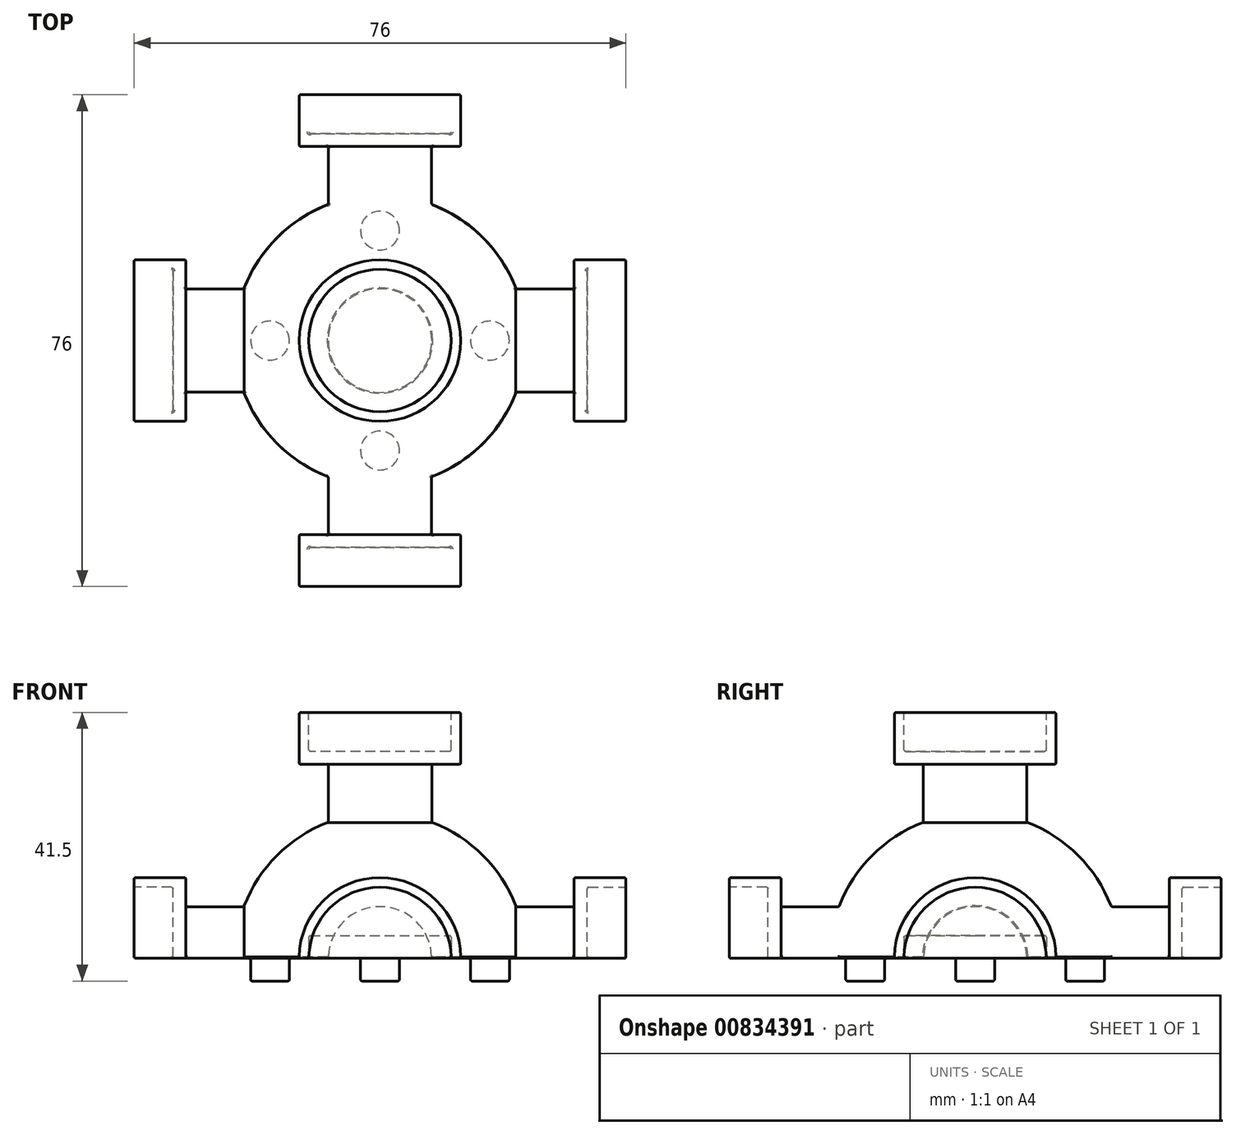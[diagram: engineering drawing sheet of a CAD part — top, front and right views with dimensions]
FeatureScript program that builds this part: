
annotation { "Feature Type Name" : "Feature", "Feature Type Description" : "" }
export const myFeature = defineFeature(function(context is Context, id is Id, definition is map)
    precondition{}
    {
        {
            var Q0;
            Q0=qCreatedBy(makeId("Top.planeOp"),FACE);
            var sketch = newSketch(context, id + "F0", { "sketchPlane" : qUnion([Q0])});
            skCircle(sketch, "E0", {"center": v(0, 0) * mm, "radius": 22.5 * mm});
            skLineSegment(sketch, "E1", {"start": v(0, 22.5) * mm, "end": v(0, -22.5) * mm});
            skSolve(sketch);
        }
        {
            var Q0;
            {var subQ0=sQuery(id+"F0.wireOp",EDGE,"E1");Q0=makeQuery(id+"F0.imprint","IMPRINT",FACE,{"disambiguationData":[TD([[makeQuery(id+"F0.imprint","IMPRINT",EDGE,{"derivedFrom":subQ0}),1.0]])]});}
            var Q1;
            Q1=sQuery(id+"F0.wireOp",EDGE,"E1");
            revolve(context, id + "F1", {"surfaceOperationType" : NewSurfaceOperationType.NEW, "entities" : qUnion([Q0]), "axis" : qUnion([Q1]), "revolveType" : RevolveType.ONE_DIRECTION, "angle" : 180 * degree});
        }
        {
            var Q0;
            Q0=makeQuery(id+"F1.opRevolve","CAP_FACE",FACE,{"disambiguationData":[OSD([sQuery(id+"F0.wireOp",EDGE,"E0"),sQuery(id+"F0.wireOp",EDGE,"E1")])],"isStart":true});
            var sketch = newSketch(context, id + "F2", { "sketchPlane" : qUnion([Q0])});
            skCircle(sketch, "E2", {"center": v(0, 0) * mm, "radius": 11 * mm});
            skSolve(sketch);
        }
        {
            var Q0;
            Q0 = qSketchRegion(id + "F2", true);
            extrude(context, id + "F3", {"entities" : qUnion([Q0]), "operationType" : NewBodyOperationType.REMOVE, "oppositeDirection" : true, "depth" : 3.5 * mm, "offsetDistance" : 25 * mm});
        }
        {
            var Q0;
            Q0=makeQuery(id+"F1.opRevolve","CAP_FACE",FACE,{"disambiguationData":[OSD([sQuery(id+"F0.wireOp",EDGE,"E0"),sQuery(id+"F0.wireOp",EDGE,"E1")])],"isStart":true});
            var sketch = newSketch(context, id + "F4", { "sketchPlane" : qUnion([Q0])});
            skCircle(sketch, "E3", {"center": v(0, 17) * mm, "radius": 3 * mm});
            skCircle(sketch, "E4", {"center": v(17, 0) * mm, "radius": 3 * mm});
            skCircle(sketch, "E5.MirrorC", {"center": v(-17, 0) * mm, "radius": 3 * mm});
            skCircle(sketch, "E6.MirrorC", {"center": v(0, -17) * mm, "radius": 3 * mm});
            skPoint(sketch, "E7.orphan", {"position": v(0, 0) * mm});
            skSolve(sketch);
        }
        {
            var Q0;
            Q0 = qSketchRegion(id + "F4", true);
            extrude(context, id + "F5", {"entities" : qUnion([Q0]), "operationType" : NewBodyOperationType.ADD, "depth" : 3.5 * mm, "offsetDistance" : 25 * mm});
        }
        {
            var Q0;
            Q0=qCreatedBy(makeId("Top.planeOp"),FACE);
            cPlane(context, id + "F6", {"entities" : qUnion([Q0]), "cplaneType" : CPlaneType.OFFSET, "offset" : 20 * mm, "width" : 150 * mm, "height" : 150 * mm});
        }
        {
            var Q0;
            Q0=qCreatedBy(id+"F6.planeOp",FACE);
            var sketch = newSketch(context, id + "F7", { "sketchPlane" : qUnion([Q0])});
            skCircle(sketch, "E8", {"center": v(0, 0) * mm, "radius": 8 * mm});
            skSolve(sketch);
        }
        {
            var Q0;
            Q0 = qSketchRegion(id + "F7", true);
            extrude(context, id + "F8", {"entities" : qUnion([Q0]), "operationType" : NewBodyOperationType.ADD, "depth" : 10 * mm, "offsetDistance" : 25 * mm});
        }
        {
            var Q0;
            Q0=makeQuery(id+"F8.opExtrude","CAP_FACE",FACE,{"disambiguationData":[OSD([sQuery(id+"F7.wireOp",EDGE,"E8")])],"isStart":false});
            var sketch = newSketch(context, id + "F9", { "sketchPlane" : qUnion([Q0])});
            skCircle(sketch, "E9", {"center": v(0, 0) * mm, "radius": 12.5 * mm});
            skSolve(sketch);
        }
        {
            var Q0;
            Q0 = qSketchRegion(id + "F9", true);
            extrude(context, id + "F10", {"entities" : qUnion([Q0]), "operationType" : NewBodyOperationType.ADD, "depth" : 8 * mm, "offsetDistance" : 25 * mm});
        }
        {
            var Q0;
            Q0=makeQuery(id+"F10.opExtrude","CAP_FACE",FACE,{"disambiguationData":[OSD([sQuery(id+"F9.wireOp",EDGE,"E9")])],"isStart":false});
            var sketch = newSketch(context, id + "F11", { "sketchPlane" : qUnion([Q0])});
            skCircle(sketch, "E10", {"center": v(0, 0) * mm, "radius": 11 * mm});
            skSolve(sketch);
        }
        {
            var Q0;
            Q0 = qSketchRegion(id + "F11", true);
            extrude(context, id + "F12", {"entities" : qUnion([Q0]), "operationType" : NewBodyOperationType.REMOVE, "oppositeDirection" : true, "depth" : 6 * mm, "offsetDistance" : 25 * mm});
        }
        {
            var Q0;
            Q0=qCreatedBy(makeId("Right.planeOp"),FACE);
            cPlane(context, id + "F13", {"entities" : qUnion([Q0]), "cplaneType" : CPlaneType.OFFSET, "offset" : 20 * mm, "width" : 150 * mm, "height" : 150 * mm});
        }
        {
            var Q0;
            Q0=qCreatedBy(id+"F13.planeOp",FACE);
            var sketch = newSketch(context, id + "F14", { "sketchPlane" : qUnion([Q0])});
            skArc(sketch, "E11", {"start": v(8, 0) * mm, "mid": v(0, 8) * mm, "end": v(-8, 0) * mm});
            skLineSegment(sketch, "E12", {"start": v(-8, 0) * mm, "end": v(8, 0) * mm});
            skSolve(sketch);
        }
        {
            var Q0;
            Q0 = qSketchRegion(id + "F14", true);
            extrude(context, id + "F15", {"entities" : qUnion([Q0]), "operationType" : NewBodyOperationType.ADD, "depth" : 10 * mm, "offsetDistance" : 25 * mm});
        }
        {
            var Q0;
            Q0=makeQuery(id+"F15.opExtrude","CAP_FACE",FACE,{"disambiguationData":[OSD([sQuery(id+"F14.wireOp",EDGE,"E11"),sQuery(id+"F14.wireOp",EDGE,"E12")])],"isStart":false});
            var sketch = newSketch(context, id + "F16", { "sketchPlane" : qUnion([Q0])});
            skArc(sketch, "E13", {"start": v(12.5, 0) * mm, "mid": v(0, 12.5) * mm, "end": v(-12.5, 0) * mm});
            skLineSegment(sketch, "E14", {"start": v(-12.5, 0) * mm, "end": v(12.5, 0) * mm});
            skSolve(sketch);
        }
        {
            var Q0;
            Q0 = qSketchRegion(id + "F16", true);
            extrude(context, id + "F17", {"entities" : qUnion([Q0]), "operationType" : NewBodyOperationType.ADD, "depth" : 8 * mm, "offsetDistance" : 25 * mm});
        }
        {
            var Q0;
            Q0=makeQuery(id+"F17.opExtrude","CAP_FACE",FACE,{"disambiguationData":[OSD([sQuery(id+"F16.wireOp",EDGE,"E13"),sQuery(id+"F16.wireOp",EDGE,"E14")])],"isStart":false});
            var sketch = newSketch(context, id + "F18", { "sketchPlane" : qUnion([Q0])});
            skArc(sketch, "E15", {"start": v(11, 0) * mm, "mid": v(0, 11) * mm, "end": v(-11, 0) * mm});
            skLineSegment(sketch, "E16", {"start": v(-11, 0) * mm, "end": v(11, 0) * mm});
            skSolve(sketch);
        }
        {
            var Q0;
            Q0 = qSketchRegion(id + "F18", true);
            extrude(context, id + "F19", {"entities" : qUnion([Q0]), "operationType" : NewBodyOperationType.REMOVE, "oppositeDirection" : true, "depth" : 6 * mm, "offsetDistance" : 25 * mm});
        }
        {
            var Q0;
            Q0=qCreatedBy(makeId("Front.planeOp"),FACE);
            cPlane(context, id + "F20", {"entities" : qUnion([Q0]), "cplaneType" : CPlaneType.OFFSET, "offset" : 20 * mm, "oppositeDirection" : true, "width" : 150 * mm, "height" : 150 * mm});
        }
        {
            var Q0;
            Q0=qCreatedBy(id+"F20.planeOp",FACE);
            var sketch = newSketch(context, id + "F21", { "sketchPlane" : qUnion([Q0])});
            skArc(sketch, "E17", {"start": v(8, 0) * mm, "mid": v(0, 8) * mm, "end": v(-8, 0) * mm});
            skLineSegment(sketch, "E18", {"start": v(8, 0) * mm, "end": v(-8, 0) * mm});
            skSolve(sketch);
        }
        {
            var Q0;
            Q0 = qSketchRegion(id + "F21", true);
            extrude(context, id + "F22", {"entities" : qUnion([Q0]), "operationType" : NewBodyOperationType.ADD, "oppositeDirection" : true, "depth" : 10 * mm, "offsetDistance" : 25 * mm});
        }
        {
            var Q0;
            Q0=makeQuery(id+"F22.opExtrude","CAP_FACE",FACE,{"disambiguationData":[OSD([sQuery(id+"F21.wireOp",EDGE,"E17"),sQuery(id+"F21.wireOp",EDGE,"E18")])],"isStart":false});
            var sketch = newSketch(context, id + "F23", { "sketchPlane" : qUnion([Q0])});
            skArc(sketch, "E19", {"start": v(12.5, 0) * mm, "mid": v(0, 12.5) * mm, "end": v(-12.5, 0) * mm});
            skLineSegment(sketch, "E20", {"start": v(-12.5, 0) * mm, "end": v(12.5, 0) * mm});
            skSolve(sketch);
        }
        {
            var Q0;
            Q0 = qSketchRegion(id + "F23", true);
            extrude(context, id + "F24", {"entities" : qUnion([Q0]), "operationType" : NewBodyOperationType.ADD, "depth" : 8 * mm, "offsetDistance" : 25 * mm});
        }
        {
            var Q0;
            Q0=makeQuery(id+"F24.opExtrude","CAP_FACE",FACE,{"disambiguationData":[OSD([sQuery(id+"F23.wireOp",EDGE,"E19"),sQuery(id+"F23.wireOp",EDGE,"E20")])],"isStart":false});
            var sketch = newSketch(context, id + "F25", { "sketchPlane" : qUnion([Q0])});
            skArc(sketch, "E21", {"start": v(11, 0) * mm, "mid": v(0, 11) * mm, "end": v(-11, 0) * mm});
            skLineSegment(sketch, "E22", {"start": v(-11, 0) * mm, "end": v(11, 0) * mm});
            skSolve(sketch);
        }
        {
            var Q0;
            Q0 = qSketchRegion(id + "F25", true);
            extrude(context, id + "F26", {"entities" : qUnion([Q0]), "operationType" : NewBodyOperationType.REMOVE, "oppositeDirection" : true, "depth" : 6 * mm, "offsetDistance" : 25 * mm});
        }
        {
            var Q0;
            Q0=qCreatedBy(makeId("Right.planeOp"),FACE);
            cPlane(context, id + "F27", {"entities" : qUnion([Q0]), "cplaneType" : CPlaneType.OFFSET, "offset" : 20 * mm, "oppositeDirection" : true, "width" : 150 * mm, "height" : 150 * mm});
        }
        {
            var Q0;
            Q0=qCreatedBy(id+"F27.planeOp",FACE);
            var sketch = newSketch(context, id + "F28", { "sketchPlane" : qUnion([Q0])});
            skArc(sketch, "E23", {"start": v(8, 0) * mm, "mid": v(0, 8) * mm, "end": v(-8, 0) * mm});
            skLineSegment(sketch, "E24", {"start": v(8, 0) * mm, "end": v(-8, 0) * mm});
            skSolve(sketch);
        }
        {
            var Q0;
            Q0 = qSketchRegion(id + "F28", true);
            extrude(context, id + "F29", {"entities" : qUnion([Q0]), "operationType" : NewBodyOperationType.ADD, "oppositeDirection" : true, "depth" : 10 * mm, "offsetDistance" : 25 * mm});
        }
        {
            var Q0;
            Q0=makeQuery(id+"F29.opExtrude","CAP_FACE",FACE,{"disambiguationData":[OSD([sQuery(id+"F28.wireOp",EDGE,"E23"),sQuery(id+"F28.wireOp",EDGE,"E24")])],"isStart":false});
            var sketch = newSketch(context, id + "F30", { "sketchPlane" : qUnion([Q0])});
            skArc(sketch, "E25", {"start": v(12.5, 0) * mm, "mid": v(0, 12.5) * mm, "end": v(-12.5, 0) * mm});
            skLineSegment(sketch, "E26", {"start": v(-12.5, 0) * mm, "end": v(12.5, 0) * mm});
            skSolve(sketch);
        }
        {
            var Q0;
            Q0 = qSketchRegion(id + "F30", true);
            extrude(context, id + "F31", {"entities" : qUnion([Q0]), "operationType" : NewBodyOperationType.ADD, "depth" : 8 * mm, "offsetDistance" : 25 * mm});
        }
        {
            var Q0;
            Q0=makeQuery(id+"F31.opExtrude","CAP_FACE",FACE,{"disambiguationData":[OSD([sQuery(id+"F30.wireOp",EDGE,"E25"),sQuery(id+"F30.wireOp",EDGE,"E26")])],"isStart":false});
            var sketch = newSketch(context, id + "F32", { "sketchPlane" : qUnion([Q0])});
            skArc(sketch, "E27", {"start": v(11, 0) * mm, "mid": v(0, 11) * mm, "end": v(-11, 0) * mm});
            skLineSegment(sketch, "E28", {"start": v(-11, 0) * mm, "end": v(11, 0) * mm});
            skSolve(sketch);
        }
        {
            var Q0;
            Q0 = qSketchRegion(id + "F32", true);
            extrude(context, id + "F33", {"entities" : qUnion([Q0]), "operationType" : NewBodyOperationType.REMOVE, "oppositeDirection" : true, "depth" : 6 * mm, "offsetDistance" : 25 * mm});
        }
        {
            var Q0;
            Q0=qCreatedBy(makeId("Front.planeOp"),FACE);
            cPlane(context, id + "F34", {"entities" : qUnion([Q0]), "cplaneType" : CPlaneType.OFFSET, "offset" : 20 * mm, "width" : 150 * mm, "height" : 150 * mm});
        }
        {
            var Q0;
            Q0=qCreatedBy(id+"F34.planeOp",FACE);
            var sketch = newSketch(context, id + "F35", { "sketchPlane" : qUnion([Q0])});
            skArc(sketch, "E29", {"start": v(8, 0) * mm, "mid": v(0, 8) * mm, "end": v(-8, 0) * mm});
            skLineSegment(sketch, "E30", {"start": v(-8, 0) * mm, "end": v(8, 0) * mm});
            skSolve(sketch);
        }
        {
            var Q0;
            Q0 = qSketchRegion(id + "F35", true);
            extrude(context, id + "F36", {"entities" : qUnion([Q0]), "operationType" : NewBodyOperationType.ADD, "depth" : 10 * mm, "offsetDistance" : 25 * mm});
        }
        {
            var Q0;
            Q0=makeQuery(id+"F36.opExtrude","CAP_FACE",FACE,{"disambiguationData":[OSD([sQuery(id+"F35.wireOp",EDGE,"E29"),sQuery(id+"F35.wireOp",EDGE,"E30")])],"isStart":false});
            var sketch = newSketch(context, id + "F37", { "sketchPlane" : qUnion([Q0])});
            skArc(sketch, "E31", {"start": v(12.5, 0) * mm, "mid": v(0, 12.5) * mm, "end": v(-12.5, 0) * mm});
            skLineSegment(sketch, "E32", {"start": v(-12.5, 0) * mm, "end": v(12.5, 0) * mm});
            skSolve(sketch);
        }
        {
            var Q0;
            Q0 = qSketchRegion(id + "F37", true);
            extrude(context, id + "F38", {"entities" : qUnion([Q0]), "operationType" : NewBodyOperationType.ADD, "depth" : 8 * mm, "offsetDistance" : 25 * mm});
        }
        {
            var Q0;
            Q0=makeQuery(id+"F38.opExtrude","CAP_FACE",FACE,{"disambiguationData":[OSD([sQuery(id+"F37.wireOp",EDGE,"E31"),sQuery(id+"F37.wireOp",EDGE,"E32")])],"isStart":false});
            var sketch = newSketch(context, id + "F39", { "sketchPlane" : qUnion([Q0])});
            skArc(sketch, "E33", {"start": v(11, 0) * mm, "mid": v(0, 11) * mm, "end": v(-11, 0) * mm});
            skLineSegment(sketch, "E34", {"start": v(-11, 0) * mm, "end": v(11, 0) * mm});
            skSolve(sketch);
        }
        {
            var Q0;
            Q0 = qSketchRegion(id + "F39", true);
            extrude(context, id + "F40", {"entities" : qUnion([Q0]), "operationType" : NewBodyOperationType.REMOVE, "oppositeDirection" : true, "depth" : 6 * mm, "offsetDistance" : 25 * mm});
        }
        {
            var Q0;
            Q0=makeQuery(id+"F31.opExtrude","SWEPT_FACE",FACE,{"disambiguationData":[OSD([sQuery(id+"F30.wireOp",EDGE,"E25")])]});
            var Q1;
            Q1=makeQuery(id+"F31.opExtrude","CAP_FACE",FACE,{"disambiguationData":[OSD([sQuery(id+"F30.wireOp",EDGE,"E25"),sQuery(id+"F30.wireOp",EDGE,"E26")])],"isStart":true});
            var Q2;
            Q2=makeQuery(id+"F24.opExtrude","CAP_FACE",FACE,{"disambiguationData":[OSD([sQuery(id+"F23.wireOp",EDGE,"E19"),sQuery(id+"F23.wireOp",EDGE,"E20")])],"isStart":false});
            var Q3;
            Q3=makeQuery(id+"F29.boolean.opBoolean","INTERSECT",EDGE,{"derivedFrom":[makeQuery(id+"F1.opRevolve","SWEPT_FACE",FACE,{"disambiguationData":[OSD([sQuery(id+"F0.wireOp",EDGE,"E0")])]}),makeQuery(id+"F29.opExtrude","SWEPT_FACE",FACE,{"disambiguationData":[OSD([sQuery(id+"F28.wireOp",EDGE,"E23")])]})]});
            var Q4;
            Q4=makeQuery(id+"F29.opExtrude","SWEPT_FACE",FACE,{"disambiguationData":[OSD([sQuery(id+"F28.wireOp",EDGE,"E23")])]});
            var Q5;
            {var subQ0=sQuery(id+"F0.wireOp",EDGE,"E0");Q5=makeQuery(id+"F29.boolean.opBoolean","SPLIT",EDGE,{"disambiguationData":[TD([makeQuery(id+"F22.opExtrude","SWEPT_FACE",FACE,{"disambiguationData":[OSD([sQuery(id+"F21.wireOp",EDGE,"E17")])]})])],"derivedFrom":makeQuery(id+"F22.boolean.opBoolean","SPLIT",EDGE,{"disambiguationData":[OD(1.0)],"derivedFrom":makeQuery(id+"F1.opRevolve","CAP_EDGE",EDGE,{"disambiguationData":[OSD([subQ0])],"isStart":true})})});}
            var Q6;
            Q6=makeQuery(id+"F10.opExtrude","SWEPT_FACE",FACE,{"disambiguationData":[OSD([sQuery(id+"F9.wireOp",EDGE,"E9")])]});
            var Q7;
            Q7=makeQuery(id+"F12.boolean.opBoolean","COPY",EDGE,{"derivedFrom":makeQuery(id+"F12.opExtrude","CAP_EDGE",EDGE,{"disambiguationData":[OSD([sQuery(id+"F11.wireOp",EDGE,"E10")])],"isStart":true})});
            var Q8;
            Q8=makeQuery(id+"F12.boolean.opBoolean","COPY",FACE,{"derivedFrom":makeQuery(id+"F12.opExtrude","SWEPT_FACE",FACE,{"disambiguationData":[OSD([sQuery(id+"F11.wireOp",EDGE,"E10")])]})});
            var Q9;
            Q9=makeQuery(id+"F12.boolean.opBoolean","COPY",FACE,{"derivedFrom":makeQuery(id+"F12.opExtrude","CAP_FACE",FACE,{"disambiguationData":[OSD([sQuery(id+"F11.wireOp",EDGE,"E10")])],"isStart":false})});
            var Q10;
            Q10=makeQuery(id+"F10.opExtrude","CAP_FACE",FACE,{"disambiguationData":[OSD([sQuery(id+"F9.wireOp",EDGE,"E9")])],"isStart":false});
            var Q11;
            Q11=makeQuery(id+"F15.opExtrude","SWEPT_FACE",FACE,{"disambiguationData":[OSD([sQuery(id+"F14.wireOp",EDGE,"E11")])]});
            var Q12;
            Q12=makeQuery(id+"F17.opExtrude","SWEPT_FACE",FACE,{"disambiguationData":[OSD([sQuery(id+"F16.wireOp",EDGE,"E13")])]});
            var Q13;
            Q13=makeQuery(id+"F17.opExtrude","CAP_FACE",FACE,{"disambiguationData":[OSD([sQuery(id+"F16.wireOp",EDGE,"E13"),sQuery(id+"F16.wireOp",EDGE,"E14")])],"isStart":true});
            var Q14;
            Q14=makeQuery(id+"F19.boolean.opBoolean","COPY",FACE,{"derivedFrom":makeQuery(id+"F19.opExtrude","CAP_FACE",FACE,{"disambiguationData":[OSD([sQuery(id+"F18.wireOp",EDGE,"E15"),sQuery(id+"F18.wireOp",EDGE,"E16")])],"isStart":false})});
            var Q15;
            Q15=makeQuery(id+"F17.opExtrude","CAP_FACE",FACE,{"disambiguationData":[OSD([sQuery(id+"F16.wireOp",EDGE,"E13"),sQuery(id+"F16.wireOp",EDGE,"E14")])],"isStart":false});
            var Q16;
            Q16=makeQuery(id+"F22.opExtrude","SWEPT_FACE",FACE,{"disambiguationData":[OSD([sQuery(id+"F21.wireOp",EDGE,"E17")])]});
            var Q17;
            Q17=makeQuery(id+"F22.boolean.opBoolean","SPLIT",EDGE,{"disambiguationData":[OD(0.0)],"derivedFrom":makeQuery(id+"F1.opRevolve","CAP_EDGE",EDGE,{"disambiguationData":[OSD([sQuery(id+"F0.wireOp",EDGE,"E0")])],"isStart":true})});
            var Q18;
            Q18=makeQuery(id+"F24.opExtrude","SWEPT_FACE",FACE,{"disambiguationData":[OSD([sQuery(id+"F23.wireOp",EDGE,"E19")])]});
            var Q19;
            Q19=makeQuery(id+"F24.opExtrude","CAP_FACE",FACE,{"disambiguationData":[OSD([sQuery(id+"F23.wireOp",EDGE,"E19"),sQuery(id+"F23.wireOp",EDGE,"E20")])],"isStart":true});
            var Q20;
            Q20=makeQuery(id+"F31.opExtrude","CAP_FACE",FACE,{"disambiguationData":[OSD([sQuery(id+"F30.wireOp",EDGE,"E25"),sQuery(id+"F30.wireOp",EDGE,"E26")])],"isStart":false});
            var Q21;
            Q21=makeQuery(id+"F1.opRevolve","SWEPT_FACE",FACE,{"disambiguationData":[OSD([sQuery(id+"F0.wireOp",EDGE,"E0")])]});
            var Q22;
            Q22=makeQuery(id+"F36.opExtrude","SWEPT_FACE",FACE,{"disambiguationData":[OSD([sQuery(id+"F35.wireOp",EDGE,"E29")])]});
            var Q23;
            Q23=makeQuery(id+"F38.opExtrude","SWEPT_FACE",FACE,{"disambiguationData":[OSD([sQuery(id+"F37.wireOp",EDGE,"E31")])]});
            var Q24;
            Q24=makeQuery(id+"F38.opExtrude","CAP_FACE",FACE,{"disambiguationData":[OSD([sQuery(id+"F37.wireOp",EDGE,"E31"),sQuery(id+"F37.wireOp",EDGE,"E32")])],"isStart":false});
            var Q25;
            Q25=makeQuery(id+"F38.boolean.opBoolean","MERGE",FACE,{"derivedFrom":[makeQuery(id+"F36.boolean.opBoolean","MERGE",FACE,{"derivedFrom":[makeQuery(id+"F31.boolean.opBoolean","MERGE",FACE,{"derivedFrom":[makeQuery(id+"F29.boolean.opBoolean","MERGE",FACE,{"derivedFrom":[makeQuery(id+"F24.boolean.opBoolean","MERGE",FACE,{"derivedFrom":[makeQuery(id+"F22.boolean.opBoolean","MERGE",FACE,{"derivedFrom":[makeQuery(id+"F17.boolean.opBoolean","MERGE",FACE,{"derivedFrom":[makeQuery(id+"F15.boolean.opBoolean","MERGE",FACE,{"derivedFrom":[makeQuery(id+"F1.opRevolve","CAP_FACE",FACE,{"disambiguationData":[OSD([sQuery(id+"F0.wireOp",EDGE,"E0"),sQuery(id+"F0.wireOp",EDGE,"E1")])],"isStart":true}),makeQuery(id+"F15.opExtrude","SWEPT_FACE",FACE,{"disambiguationData":[OSD([sQuery(id+"F14.wireOp",EDGE,"E12")])]})]}),makeQuery(id+"F17.opExtrude","SWEPT_FACE",FACE,{"disambiguationData":[OSD([sQuery(id+"F16.wireOp",EDGE,"E14")])]})]}),makeQuery(id+"F22.opExtrude","SWEPT_FACE",FACE,{"disambiguationData":[OSD([sQuery(id+"F21.wireOp",EDGE,"E18")])]})]}),makeQuery(id+"F24.opExtrude","SWEPT_FACE",FACE,{"disambiguationData":[OSD([sQuery(id+"F23.wireOp",EDGE,"E20")])]})]}),makeQuery(id+"F29.opExtrude","SWEPT_FACE",FACE,{"disambiguationData":[OSD([sQuery(id+"F28.wireOp",EDGE,"E24")])]})]}),makeQuery(id+"F31.opExtrude","SWEPT_FACE",FACE,{"disambiguationData":[OSD([sQuery(id+"F30.wireOp",EDGE,"E26")])]})]}),makeQuery(id+"F36.opExtrude","SWEPT_FACE",FACE,{"disambiguationData":[OSD([sQuery(id+"F35.wireOp",EDGE,"E30")])]})]}),makeQuery(id+"F38.opExtrude","SWEPT_FACE",FACE,{"disambiguationData":[OSD([sQuery(id+"F37.wireOp",EDGE,"E32")])]})]});
            var Q26;
            {var subQ0=sQuery(id+"F30.wireOp",EDGE,"E26");var subQ1=sQuery(id+"F30.wireOp",EDGE,"E25");Q26=makeQuery(id+"F31.opExtrude","SWEPT_EDGE",EDGE,{"disambiguationData":[OSD([subQ1,subQ0]),TDD([makeQuery(id+"F30.imprint","INTERSECT",VERTEX,{"disambiguationData":[OD(0.0)],"derivedFrom":[subQ1,subQ0]})])]});}
            var Q27;
            {var subQ0=sQuery(id+"F30.wireOp",EDGE,"E26");var subQ1=sQuery(id+"F30.wireOp",EDGE,"E25");Q27=makeQuery(id+"F31.opExtrude","SWEPT_EDGE",EDGE,{"disambiguationData":[OSD([subQ1,subQ0]),TDD([makeQuery(id+"F30.imprint","INTERSECT",VERTEX,{"disambiguationData":[OD(1.0)],"derivedFrom":[subQ1,subQ0]})])]});}
            var Q28;
            Q28=makeQuery(id+"F31.opExtrude","CAP_EDGE",EDGE,{"disambiguationData":[OSD([sQuery(id+"F30.wireOp",EDGE,"E25")])],"isStart":true});
            var Q29;
            Q29=makeQuery(id+"F31.opExtrude","CAP_EDGE",EDGE,{"disambiguationData":[OSD([sQuery(id+"F30.wireOp",EDGE,"E25")])],"isStart":false});
            var Q30;
            Q30=makeQuery(id+"F26.boolean.opBoolean","COPY",FACE,{"derivedFrom":makeQuery(id+"F26.opExtrude","SWEPT_FACE",FACE,{"disambiguationData":[OSD([sQuery(id+"F25.wireOp",EDGE,"E21")])]})});
            var Q31;
            Q31=makeQuery(id+"F26.boolean.opBoolean","COPY",FACE,{"derivedFrom":makeQuery(id+"F26.opExtrude","CAP_FACE",FACE,{"disambiguationData":[OSD([sQuery(id+"F25.wireOp",EDGE,"E21"),sQuery(id+"F25.wireOp",EDGE,"E22")])],"isStart":false})});
            var Q32;
            {var subQ0=sQuery(id+"F28.wireOp",EDGE,"E24");var subQ1=sQuery(id+"F28.wireOp",EDGE,"E23");Q32=makeQuery(id+"F29.opExtrude","SWEPT_EDGE",EDGE,{"disambiguationData":[OSD([subQ1,subQ0]),TDD([makeQuery(id+"F28.imprint","INTERSECT",VERTEX,{"disambiguationData":[OD(0.0)],"derivedFrom":[subQ1,subQ0]})])]});}
            var Q33;
            {var subQ0=sQuery(id+"F28.wireOp",EDGE,"E24");var subQ1=sQuery(id+"F28.wireOp",EDGE,"E23");Q33=makeQuery(id+"F29.opExtrude","SWEPT_EDGE",EDGE,{"disambiguationData":[OSD([subQ1,subQ0]),TDD([makeQuery(id+"F28.imprint","INTERSECT",VERTEX,{"disambiguationData":[OD(1.0)],"derivedFrom":[subQ1,subQ0]})])]});}
            var Q34;
            Q34=makeQuery(id+"F3.boolean.opBoolean","COPY",FACE,{"derivedFrom":makeQuery(id+"F3.opExtrude","CAP_FACE",FACE,{"disambiguationData":[OSD([sQuery(id+"F2.wireOp",EDGE,"E2")])],"isStart":false})});
            var Q35;
            Q35=makeQuery(id+"F5.opExtrude","SWEPT_FACE",FACE,{"disambiguationData":[OSD([sQuery(id+"F4.wireOp",EDGE,"E3")])]});
            var Q36;
            Q36=makeQuery(id+"F5.opExtrude","CAP_FACE",FACE,{"disambiguationData":[OSD([sQuery(id+"F4.wireOp",EDGE,"E3")])],"isStart":false});
            var Q37;
            Q37=makeQuery(id+"F5.opExtrude","SWEPT_FACE",FACE,{"disambiguationData":[OSD([sQuery(id+"F4.wireOp",EDGE,"E4")])]});
            var Q38;
            Q38=makeQuery(id+"F5.opExtrude","CAP_FACE",FACE,{"disambiguationData":[OSD([sQuery(id+"F4.wireOp",EDGE,"E4")])],"isStart":false});
            var Q39;
            Q39=makeQuery(id+"F5.opExtrude","SWEPT_FACE",FACE,{"disambiguationData":[OSD([sQuery(id+"F4.wireOp",EDGE,"E5.MirrorC")])]});
            var Q40;
            Q40=makeQuery(id+"F5.opExtrude","CAP_FACE",FACE,{"disambiguationData":[OSD([sQuery(id+"F4.wireOp",EDGE,"E5.MirrorC")])],"isStart":false});
            var Q41;
            Q41=makeQuery(id+"F5.opExtrude","SWEPT_FACE",FACE,{"disambiguationData":[OSD([sQuery(id+"F4.wireOp",EDGE,"E6.MirrorC")])]});
            var Q42;
            Q42=makeQuery(id+"F5.opExtrude","CAP_FACE",FACE,{"disambiguationData":[OSD([sQuery(id+"F4.wireOp",EDGE,"E6.MirrorC")])],"isStart":false});
            var Q43;
            Q43=makeQuery(id+"F8.opExtrude","SWEPT_FACE",FACE,{"disambiguationData":[OSD([sQuery(id+"F7.wireOp",EDGE,"E8")])]});
            var Q44;
            Q44=makeQuery(id+"F10.opExtrude","CAP_EDGE",EDGE,{"disambiguationData":[OSD([sQuery(id+"F9.wireOp",EDGE,"E9")])],"isStart":false});
            var Q45;
            Q45=makeQuery(id+"F10.opExtrude","CAP_FACE",FACE,{"disambiguationData":[OSD([sQuery(id+"F9.wireOp",EDGE,"E9")])],"isStart":true});
            var Q46;
            Q46=makeQuery(id+"F12.boolean.opBoolean","COPY",EDGE,{"derivedFrom":makeQuery(id+"F12.opExtrude","CAP_EDGE",EDGE,{"disambiguationData":[OSD([sQuery(id+"F11.wireOp",EDGE,"E10")])],"isStart":false})});
            var Q47;
            Q47=makeQuery(id+"F15.boolean.opBoolean","INTERSECT",EDGE,{"derivedFrom":[makeQuery(id+"F1.opRevolve","SWEPT_FACE",FACE,{"disambiguationData":[OSD([sQuery(id+"F0.wireOp",EDGE,"E0")])]}),makeQuery(id+"F15.opExtrude","SWEPT_FACE",FACE,{"disambiguationData":[OSD([sQuery(id+"F14.wireOp",EDGE,"E11")])]})]});
            var Q48;
            {var subQ0=sQuery(id+"F14.wireOp",EDGE,"E12");var subQ1=sQuery(id+"F14.wireOp",EDGE,"E11");Q48=makeQuery(id+"F15.opExtrude","SWEPT_EDGE",EDGE,{"disambiguationData":[OSD([subQ1,subQ0]),TDD([makeQuery(id+"F14.imprint","INTERSECT",VERTEX,{"disambiguationData":[OD(0.0)],"derivedFrom":[subQ1,subQ0]})])]});}
            var Q49;
            {var subQ0=sQuery(id+"F14.wireOp",EDGE,"E12");var subQ1=sQuery(id+"F14.wireOp",EDGE,"E11");Q49=makeQuery(id+"F15.opExtrude","SWEPT_EDGE",EDGE,{"disambiguationData":[OSD([subQ1,subQ0]),TDD([makeQuery(id+"F14.imprint","INTERSECT",VERTEX,{"disambiguationData":[OD(1.0)],"derivedFrom":[subQ1,subQ0]})])]});}
            var Q50;
            {var subQ0=sQuery(id+"F16.wireOp",EDGE,"E14");var subQ1=sQuery(id+"F16.wireOp",EDGE,"E13");Q50=makeQuery(id+"F17.opExtrude","SWEPT_EDGE",EDGE,{"disambiguationData":[OSD([subQ1,subQ0]),TDD([makeQuery(id+"F16.imprint","INTERSECT",VERTEX,{"disambiguationData":[OD(0.0)],"derivedFrom":[subQ1,subQ0]})])]});}
            var Q51;
            {var subQ0=sQuery(id+"F16.wireOp",EDGE,"E14");var subQ1=sQuery(id+"F16.wireOp",EDGE,"E13");Q51=makeQuery(id+"F17.opExtrude","SWEPT_EDGE",EDGE,{"disambiguationData":[OSD([subQ1,subQ0]),TDD([makeQuery(id+"F16.imprint","INTERSECT",VERTEX,{"disambiguationData":[OD(1.0)],"derivedFrom":[subQ1,subQ0]})])]});}
            var Q52;
            Q52=makeQuery(id+"F17.opExtrude","CAP_EDGE",EDGE,{"disambiguationData":[OSD([sQuery(id+"F16.wireOp",EDGE,"E13")])],"isStart":true});
            var Q53;
            Q53=makeQuery(id+"F17.opExtrude","CAP_EDGE",EDGE,{"disambiguationData":[OSD([sQuery(id+"F16.wireOp",EDGE,"E13")])],"isStart":false});
            var Q54;
            Q54=makeQuery(id+"F19.boolean.opBoolean","COPY",FACE,{"derivedFrom":makeQuery(id+"F19.opExtrude","SWEPT_FACE",FACE,{"disambiguationData":[OSD([sQuery(id+"F18.wireOp",EDGE,"E15")])]})});
            var Q55;
            Q55=makeQuery(id+"F22.boolean.opBoolean","INTERSECT",EDGE,{"derivedFrom":[makeQuery(id+"F1.opRevolve","SWEPT_FACE",FACE,{"disambiguationData":[OSD([sQuery(id+"F0.wireOp",EDGE,"E0")])]}),makeQuery(id+"F22.opExtrude","SWEPT_FACE",FACE,{"disambiguationData":[OSD([sQuery(id+"F21.wireOp",EDGE,"E17")])]})]});
            var Q56;
            {var subQ0=sQuery(id+"F21.wireOp",EDGE,"E18");var subQ1=sQuery(id+"F21.wireOp",EDGE,"E17");Q56=makeQuery(id+"F22.opExtrude","SWEPT_EDGE",EDGE,{"disambiguationData":[OSD([subQ1,subQ0]),TDD([makeQuery(id+"F21.imprint","INTERSECT",VERTEX,{"disambiguationData":[OD(0.0)],"derivedFrom":[subQ1,subQ0]})])]});}
            var Q57;
            {var subQ0=sQuery(id+"F21.wireOp",EDGE,"E18");var subQ1=sQuery(id+"F21.wireOp",EDGE,"E17");Q57=makeQuery(id+"F22.opExtrude","SWEPT_EDGE",EDGE,{"disambiguationData":[OSD([subQ1,subQ0]),TDD([makeQuery(id+"F21.imprint","INTERSECT",VERTEX,{"disambiguationData":[OD(1.0)],"derivedFrom":[subQ1,subQ0]})])]});}
            var Q58;
            {var subQ0=sQuery(id+"F23.wireOp",EDGE,"E20");var subQ1=sQuery(id+"F23.wireOp",EDGE,"E19");Q58=makeQuery(id+"F24.opExtrude","SWEPT_EDGE",EDGE,{"disambiguationData":[OSD([subQ1,subQ0]),TDD([makeQuery(id+"F23.imprint","INTERSECT",VERTEX,{"disambiguationData":[OD(0.0)],"derivedFrom":[subQ1,subQ0]})])]});}
            var Q59;
            {var subQ0=sQuery(id+"F23.wireOp",EDGE,"E20");var subQ1=sQuery(id+"F23.wireOp",EDGE,"E19");Q59=makeQuery(id+"F24.opExtrude","SWEPT_EDGE",EDGE,{"disambiguationData":[OSD([subQ1,subQ0]),TDD([makeQuery(id+"F23.imprint","INTERSECT",VERTEX,{"disambiguationData":[OD(1.0)],"derivedFrom":[subQ1,subQ0]})])]});}
            var Q60;
            Q60=makeQuery(id+"F24.opExtrude","CAP_EDGE",EDGE,{"disambiguationData":[OSD([sQuery(id+"F23.wireOp",EDGE,"E19")])],"isStart":true});
            var Q61;
            Q61=makeQuery(id+"F24.opExtrude","CAP_EDGE",EDGE,{"disambiguationData":[OSD([sQuery(id+"F23.wireOp",EDGE,"E19")])],"isStart":false});
            var Q62;
            Q62=makeQuery(id+"F33.boolean.opBoolean","COPY",FACE,{"derivedFrom":makeQuery(id+"F33.opExtrude","SWEPT_FACE",FACE,{"disambiguationData":[OSD([sQuery(id+"F32.wireOp",EDGE,"E27")])]})});
            var Q63;
            Q63=makeQuery(id+"F33.boolean.opBoolean","COPY",FACE,{"derivedFrom":makeQuery(id+"F33.opExtrude","CAP_FACE",FACE,{"disambiguationData":[OSD([sQuery(id+"F32.wireOp",EDGE,"E27"),sQuery(id+"F32.wireOp",EDGE,"E28")])],"isStart":false})});
            var Q64;
            Q64=makeQuery(id+"F36.boolean.opBoolean","INTERSECT",EDGE,{"derivedFrom":[makeQuery(id+"F1.opRevolve","SWEPT_FACE",FACE,{"disambiguationData":[OSD([sQuery(id+"F0.wireOp",EDGE,"E0")])]}),makeQuery(id+"F36.opExtrude","SWEPT_FACE",FACE,{"disambiguationData":[OSD([sQuery(id+"F35.wireOp",EDGE,"E29")])]})]});
            var Q65;
            {var subQ0=sQuery(id+"F35.wireOp",EDGE,"E30");var subQ1=sQuery(id+"F35.wireOp",EDGE,"E29");Q65=makeQuery(id+"F36.opExtrude","SWEPT_EDGE",EDGE,{"disambiguationData":[OSD([subQ1,subQ0]),TDD([makeQuery(id+"F35.imprint","INTERSECT",VERTEX,{"disambiguationData":[OD(0.0)],"derivedFrom":[subQ1,subQ0]})])]});}
            var Q66;
            {var subQ0=sQuery(id+"F35.wireOp",EDGE,"E30");var subQ1=sQuery(id+"F35.wireOp",EDGE,"E29");Q66=makeQuery(id+"F36.opExtrude","SWEPT_EDGE",EDGE,{"disambiguationData":[OSD([subQ1,subQ0]),TDD([makeQuery(id+"F35.imprint","INTERSECT",VERTEX,{"disambiguationData":[OD(1.0)],"derivedFrom":[subQ1,subQ0]})])]});}
            var Q67;
            {var subQ0=sQuery(id+"F0.wireOp",EDGE,"E0");var subQ7=makeQuery(id+"F15.opExtrude","SWEPT_FACE",FACE,{"disambiguationData":[OSD([sQuery(id+"F14.wireOp",EDGE,"E11")])]});Q67=makeQuery(id+"F36.boolean.opBoolean","SPLIT",EDGE,{"disambiguationData":[TD([subQ7])],"derivedFrom":makeQuery(id+"F29.boolean.opBoolean","SPLIT",EDGE,{"disambiguationData":[TD([subQ7])],"derivedFrom":makeQuery(id+"F22.boolean.opBoolean","SPLIT",EDGE,{"disambiguationData":[OD(1.0)],"derivedFrom":makeQuery(id+"F1.opRevolve","CAP_EDGE",EDGE,{"disambiguationData":[OSD([subQ0])],"isStart":true})})})});}
            var Q68;
            {var subQ0=sQuery(id+"F0.wireOp",EDGE,"E0");var subQ2=makeQuery(id+"F29.opExtrude","SWEPT_FACE",FACE,{"disambiguationData":[OSD([sQuery(id+"F28.wireOp",EDGE,"E23")])]});Q68=makeQuery(id+"F36.boolean.opBoolean","SPLIT",EDGE,{"disambiguationData":[TD([subQ2])],"derivedFrom":makeQuery(id+"F29.boolean.opBoolean","SPLIT",EDGE,{"disambiguationData":[TD([makeQuery(id+"F15.opExtrude","SWEPT_FACE",FACE,{"disambiguationData":[OSD([sQuery(id+"F14.wireOp",EDGE,"E11")])]})])],"derivedFrom":makeQuery(id+"F22.boolean.opBoolean","SPLIT",EDGE,{"disambiguationData":[OD(1.0)],"derivedFrom":makeQuery(id+"F1.opRevolve","CAP_EDGE",EDGE,{"disambiguationData":[OSD([subQ0])],"isStart":true})})})});}
            var Q69;
            {var subQ0=sQuery(id+"F37.wireOp",EDGE,"E32");var subQ1=sQuery(id+"F37.wireOp",EDGE,"E31");Q69=makeQuery(id+"F38.opExtrude","SWEPT_EDGE",EDGE,{"disambiguationData":[OSD([subQ1,subQ0]),TDD([makeQuery(id+"F37.imprint","INTERSECT",VERTEX,{"disambiguationData":[OD(0.0)],"derivedFrom":[subQ1,subQ0]})])]});}
            var Q70;
            {var subQ0=sQuery(id+"F37.wireOp",EDGE,"E32");var subQ1=sQuery(id+"F37.wireOp",EDGE,"E31");Q70=makeQuery(id+"F38.opExtrude","SWEPT_EDGE",EDGE,{"disambiguationData":[OSD([subQ1,subQ0]),TDD([makeQuery(id+"F37.imprint","INTERSECT",VERTEX,{"disambiguationData":[OD(1.0)],"derivedFrom":[subQ1,subQ0]})])]});}
            var Q71;
            Q71=makeQuery(id+"F38.opExtrude","CAP_EDGE",EDGE,{"disambiguationData":[OSD([sQuery(id+"F37.wireOp",EDGE,"E31")])],"isStart":false});
            var Q72;
            Q72=makeQuery(id+"F38.opExtrude","CAP_FACE",FACE,{"disambiguationData":[OSD([sQuery(id+"F37.wireOp",EDGE,"E31"),sQuery(id+"F37.wireOp",EDGE,"E32")])],"isStart":true});
            var Q73;
            Q73=makeQuery(id+"F40.boolean.opBoolean","COPY",FACE,{"derivedFrom":makeQuery(id+"F40.opExtrude","SWEPT_FACE",FACE,{"disambiguationData":[OSD([sQuery(id+"F39.wireOp",EDGE,"E33")])]})});
            var Q74;
            Q74=makeQuery(id+"F40.boolean.opBoolean","COPY",FACE,{"derivedFrom":makeQuery(id+"F40.opExtrude","CAP_FACE",FACE,{"disambiguationData":[OSD([sQuery(id+"F39.wireOp",EDGE,"E33"),sQuery(id+"F39.wireOp",EDGE,"E34")])],"isStart":false})});
            var Q75;
            Q75=makeQuery(id+"F29.opExtrude","CAP_EDGE",EDGE,{"disambiguationData":[OSD([sQuery(id+"F28.wireOp",EDGE,"E23")])],"isStart":false});
            var Q76;
            Q76=makeQuery(id+"F31.boolean.opBoolean","SPLIT",EDGE,{"disambiguationData":[OD(0.0)],"derivedFrom":makeQuery(id+"F31.opExtrude","CAP_EDGE",EDGE,{"disambiguationData":[OSD([sQuery(id+"F30.wireOp",EDGE,"E26")])],"isStart":true})});
            var Q77;
            Q77=makeQuery(id+"F31.boolean.opBoolean","SPLIT",EDGE,{"disambiguationData":[OD(1.0)],"derivedFrom":makeQuery(id+"F31.opExtrude","CAP_EDGE",EDGE,{"disambiguationData":[OSD([sQuery(id+"F30.wireOp",EDGE,"E26")])],"isStart":true})});
            var Q78;
            {var subQ0=sQuery(id+"F25.wireOp",EDGE,"E22");var subQ1=sQuery(id+"F25.wireOp",EDGE,"E21");var subQ2=sQuery(id+"F23.wireOp",EDGE,"E20");Q78=makeQuery(id+"F26.boolean.opBoolean","COPY",EDGE,{"derivedFrom":makeQuery(id+"F26.opExtrude","SWEPT_EDGE",EDGE,{"disambiguationData":[OSD([subQ2,subQ1,subQ0]),TDD([makeQuery(id+"F25.imprint","INTERSECT",VERTEX,{"disambiguationData":[OD(0.0)],"derivedFrom":[makeQuery(id+"F24.opExtrude","CAP_EDGE",EDGE,{"disambiguationData":[OSD([subQ2])],"isStart":false}),subQ1,subQ0]})])]})});}
            var Q79;
            {var subQ0=sQuery(id+"F25.wireOp",EDGE,"E22");var subQ1=sQuery(id+"F25.wireOp",EDGE,"E21");var subQ2=sQuery(id+"F23.wireOp",EDGE,"E20");Q79=makeQuery(id+"F26.boolean.opBoolean","COPY",EDGE,{"derivedFrom":makeQuery(id+"F26.opExtrude","SWEPT_EDGE",EDGE,{"disambiguationData":[OSD([subQ2,subQ1,subQ0]),TDD([makeQuery(id+"F25.imprint","INTERSECT",VERTEX,{"disambiguationData":[OD(1.0)],"derivedFrom":[makeQuery(id+"F24.opExtrude","CAP_EDGE",EDGE,{"disambiguationData":[OSD([subQ2])],"isStart":false}),subQ1,subQ0]})])]})});}
            var Q80;
            Q80=makeQuery(id+"F26.boolean.opBoolean","COPY",EDGE,{"derivedFrom":makeQuery(id+"F26.opExtrude","CAP_EDGE",EDGE,{"disambiguationData":[OSD([sQuery(id+"F25.wireOp",EDGE,"E21")])],"isStart":true})});
            var Q81;
            Q81=makeQuery(id+"F26.boolean.opBoolean","COPY",EDGE,{"derivedFrom":makeQuery(id+"F26.opExtrude","CAP_EDGE",EDGE,{"disambiguationData":[OSD([sQuery(id+"F25.wireOp",EDGE,"E21")])],"isStart":false})});
            var Q82;
            Q82=makeQuery(id+"F26.boolean.opBoolean","SPLIT",EDGE,{"disambiguationData":[OD(0.0)],"derivedFrom":makeQuery(id+"F24.opExtrude","CAP_EDGE",EDGE,{"disambiguationData":[OSD([sQuery(id+"F23.wireOp",EDGE,"E20")])],"isStart":false})});
            var Q83;
            Q83=makeQuery(id+"F26.boolean.opBoolean","SPLIT",EDGE,{"disambiguationData":[OD(1.0)],"derivedFrom":makeQuery(id+"F24.opExtrude","CAP_EDGE",EDGE,{"disambiguationData":[OSD([sQuery(id+"F23.wireOp",EDGE,"E20")])],"isStart":false})});
            var Q84;
            Q84=makeQuery(id+"F3.boolean.opBoolean","COPY",FACE,{"derivedFrom":makeQuery(id+"F3.opExtrude","SWEPT_FACE",FACE,{"disambiguationData":[OSD([sQuery(id+"F2.wireOp",EDGE,"E2")])]})});
            var Q85;
            Q85=makeQuery(id+"F3.boolean.opBoolean","COPY",EDGE,{"derivedFrom":makeQuery(id+"F3.opExtrude","CAP_EDGE",EDGE,{"disambiguationData":[OSD([sQuery(id+"F2.wireOp",EDGE,"E2")])],"isStart":false})});
            var Q86;
            Q86=makeQuery(id+"F5.opExtrude","CAP_EDGE",EDGE,{"disambiguationData":[OSD([sQuery(id+"F4.wireOp",EDGE,"E3")])],"isStart":true});
            var Q87;
            Q87=makeQuery(id+"F5.opExtrude","CAP_EDGE",EDGE,{"disambiguationData":[OSD([sQuery(id+"F4.wireOp",EDGE,"E4")])],"isStart":true});
            var Q88;
            Q88=makeQuery(id+"F5.opExtrude","CAP_EDGE",EDGE,{"disambiguationData":[OSD([sQuery(id+"F4.wireOp",EDGE,"E5.MirrorC")])],"isStart":true});
            var Q89;
            Q89=makeQuery(id+"F5.opExtrude","CAP_EDGE",EDGE,{"disambiguationData":[OSD([sQuery(id+"F4.wireOp",EDGE,"E6.MirrorC")])],"isStart":true});
            var Q90;
            Q90=makeQuery(id+"F10.opExtrude","CAP_EDGE",EDGE,{"disambiguationData":[OSD([sQuery(id+"F9.wireOp",EDGE,"E9")])],"isStart":true});
            var Q91;
            Q91=makeQuery(id+"F8.opExtrude","CAP_EDGE",EDGE,{"disambiguationData":[OSD([sQuery(id+"F7.wireOp",EDGE,"E8")])],"isStart":false});
            var Q92;
            Q92=makeQuery(id+"F15.opExtrude","CAP_EDGE",EDGE,{"disambiguationData":[OSD([sQuery(id+"F14.wireOp",EDGE,"E11")])],"isStart":false});
            var Q93;
            Q93=makeQuery(id+"F17.boolean.opBoolean","SPLIT",EDGE,{"disambiguationData":[OD(0.0)],"derivedFrom":makeQuery(id+"F17.opExtrude","CAP_EDGE",EDGE,{"disambiguationData":[OSD([sQuery(id+"F16.wireOp",EDGE,"E14")])],"isStart":true})});
            var Q94;
            Q94=makeQuery(id+"F17.boolean.opBoolean","SPLIT",EDGE,{"disambiguationData":[OD(1.0)],"derivedFrom":makeQuery(id+"F17.opExtrude","CAP_EDGE",EDGE,{"disambiguationData":[OSD([sQuery(id+"F16.wireOp",EDGE,"E14")])],"isStart":true})});
            var Q95;
            {var subQ0=sQuery(id+"F18.wireOp",EDGE,"E16");var subQ1=sQuery(id+"F18.wireOp",EDGE,"E15");var subQ2=sQuery(id+"F16.wireOp",EDGE,"E14");Q95=makeQuery(id+"F19.boolean.opBoolean","COPY",EDGE,{"derivedFrom":makeQuery(id+"F19.opExtrude","SWEPT_EDGE",EDGE,{"disambiguationData":[OSD([subQ2,subQ1,subQ0]),TDD([makeQuery(id+"F18.imprint","INTERSECT",VERTEX,{"disambiguationData":[OD(0.0)],"derivedFrom":[makeQuery(id+"F17.opExtrude","CAP_EDGE",EDGE,{"disambiguationData":[OSD([subQ2])],"isStart":false}),subQ1,subQ0]})])]})});}
            var Q96;
            {var subQ0=sQuery(id+"F18.wireOp",EDGE,"E16");var subQ1=sQuery(id+"F18.wireOp",EDGE,"E15");var subQ2=sQuery(id+"F16.wireOp",EDGE,"E14");Q96=makeQuery(id+"F19.boolean.opBoolean","COPY",EDGE,{"derivedFrom":makeQuery(id+"F19.opExtrude","SWEPT_EDGE",EDGE,{"disambiguationData":[OSD([subQ2,subQ1,subQ0]),TDD([makeQuery(id+"F18.imprint","INTERSECT",VERTEX,{"disambiguationData":[OD(1.0)],"derivedFrom":[makeQuery(id+"F17.opExtrude","CAP_EDGE",EDGE,{"disambiguationData":[OSD([subQ2])],"isStart":false}),subQ1,subQ0]})])]})});}
            var Q97;
            Q97=makeQuery(id+"F19.boolean.opBoolean","COPY",EDGE,{"derivedFrom":makeQuery(id+"F19.opExtrude","CAP_EDGE",EDGE,{"disambiguationData":[OSD([sQuery(id+"F18.wireOp",EDGE,"E15")])],"isStart":true})});
            var Q98;
            Q98=makeQuery(id+"F19.boolean.opBoolean","COPY",EDGE,{"derivedFrom":makeQuery(id+"F19.opExtrude","CAP_EDGE",EDGE,{"disambiguationData":[OSD([sQuery(id+"F18.wireOp",EDGE,"E15")])],"isStart":false})});
            var Q99;
            Q99=makeQuery(id+"F19.boolean.opBoolean","SPLIT",EDGE,{"disambiguationData":[OD(0.0)],"derivedFrom":makeQuery(id+"F17.opExtrude","CAP_EDGE",EDGE,{"disambiguationData":[OSD([sQuery(id+"F16.wireOp",EDGE,"E14")])],"isStart":false})});
            var Q100;
            Q100=makeQuery(id+"F19.boolean.opBoolean","SPLIT",EDGE,{"disambiguationData":[OD(1.0)],"derivedFrom":makeQuery(id+"F17.opExtrude","CAP_EDGE",EDGE,{"disambiguationData":[OSD([sQuery(id+"F16.wireOp",EDGE,"E14")])],"isStart":false})});
            var Q101;
            Q101=makeQuery(id+"F22.opExtrude","CAP_EDGE",EDGE,{"disambiguationData":[OSD([sQuery(id+"F21.wireOp",EDGE,"E17")])],"isStart":false});
            var Q102;
            Q102=makeQuery(id+"F24.boolean.opBoolean","SPLIT",EDGE,{"disambiguationData":[OD(0.0)],"derivedFrom":makeQuery(id+"F24.opExtrude","CAP_EDGE",EDGE,{"disambiguationData":[OSD([sQuery(id+"F23.wireOp",EDGE,"E20")])],"isStart":true})});
            var Q103;
            Q103=makeQuery(id+"F24.boolean.opBoolean","SPLIT",EDGE,{"disambiguationData":[OD(1.0)],"derivedFrom":makeQuery(id+"F24.opExtrude","CAP_EDGE",EDGE,{"disambiguationData":[OSD([sQuery(id+"F23.wireOp",EDGE,"E20")])],"isStart":true})});
            var Q104;
            {var subQ0=sQuery(id+"F32.wireOp",EDGE,"E28");var subQ1=sQuery(id+"F32.wireOp",EDGE,"E27");var subQ2=sQuery(id+"F30.wireOp",EDGE,"E26");Q104=makeQuery(id+"F33.boolean.opBoolean","COPY",EDGE,{"derivedFrom":makeQuery(id+"F33.opExtrude","SWEPT_EDGE",EDGE,{"disambiguationData":[OSD([subQ2,subQ1,subQ0]),TDD([makeQuery(id+"F32.imprint","INTERSECT",VERTEX,{"disambiguationData":[OD(0.0)],"derivedFrom":[makeQuery(id+"F31.opExtrude","CAP_EDGE",EDGE,{"disambiguationData":[OSD([subQ2])],"isStart":false}),subQ1,subQ0]})])]})});}
            var Q105;
            {var subQ0=sQuery(id+"F32.wireOp",EDGE,"E28");var subQ1=sQuery(id+"F32.wireOp",EDGE,"E27");var subQ2=sQuery(id+"F30.wireOp",EDGE,"E26");Q105=makeQuery(id+"F33.boolean.opBoolean","COPY",EDGE,{"derivedFrom":makeQuery(id+"F33.opExtrude","SWEPT_EDGE",EDGE,{"disambiguationData":[OSD([subQ2,subQ1,subQ0]),TDD([makeQuery(id+"F32.imprint","INTERSECT",VERTEX,{"disambiguationData":[OD(1.0)],"derivedFrom":[makeQuery(id+"F31.opExtrude","CAP_EDGE",EDGE,{"disambiguationData":[OSD([subQ2])],"isStart":false}),subQ1,subQ0]})])]})});}
            var Q106;
            Q106=makeQuery(id+"F33.boolean.opBoolean","COPY",EDGE,{"derivedFrom":makeQuery(id+"F33.opExtrude","CAP_EDGE",EDGE,{"disambiguationData":[OSD([sQuery(id+"F32.wireOp",EDGE,"E27")])],"isStart":true})});
            var Q107;
            Q107=makeQuery(id+"F33.boolean.opBoolean","COPY",EDGE,{"derivedFrom":makeQuery(id+"F33.opExtrude","CAP_EDGE",EDGE,{"disambiguationData":[OSD([sQuery(id+"F32.wireOp",EDGE,"E27")])],"isStart":false})});
            var Q108;
            Q108=makeQuery(id+"F33.boolean.opBoolean","SPLIT",EDGE,{"disambiguationData":[OD(0.0)],"derivedFrom":makeQuery(id+"F31.opExtrude","CAP_EDGE",EDGE,{"disambiguationData":[OSD([sQuery(id+"F30.wireOp",EDGE,"E26")])],"isStart":false})});
            var Q109;
            Q109=makeQuery(id+"F33.boolean.opBoolean","SPLIT",EDGE,{"disambiguationData":[OD(1.0)],"derivedFrom":makeQuery(id+"F31.opExtrude","CAP_EDGE",EDGE,{"disambiguationData":[OSD([sQuery(id+"F30.wireOp",EDGE,"E26")])],"isStart":false})});
            var Q110;
            Q110=makeQuery(id+"F38.opExtrude","CAP_EDGE",EDGE,{"disambiguationData":[OSD([sQuery(id+"F37.wireOp",EDGE,"E31")])],"isStart":true});
            var Q111;
            {var subQ0=sQuery(id+"F39.wireOp",EDGE,"E34");var subQ1=sQuery(id+"F39.wireOp",EDGE,"E33");var subQ2=sQuery(id+"F37.wireOp",EDGE,"E32");Q111=makeQuery(id+"F40.boolean.opBoolean","COPY",EDGE,{"derivedFrom":makeQuery(id+"F40.opExtrude","SWEPT_EDGE",EDGE,{"disambiguationData":[OSD([subQ2,subQ1,subQ0]),TDD([makeQuery(id+"F39.imprint","INTERSECT",VERTEX,{"disambiguationData":[OD(0.0)],"derivedFrom":[makeQuery(id+"F38.opExtrude","CAP_EDGE",EDGE,{"disambiguationData":[OSD([subQ2])],"isStart":false}),subQ1,subQ0]})])]})});}
            var Q112;
            {var subQ0=sQuery(id+"F39.wireOp",EDGE,"E34");var subQ1=sQuery(id+"F39.wireOp",EDGE,"E33");var subQ2=sQuery(id+"F37.wireOp",EDGE,"E32");Q112=makeQuery(id+"F40.boolean.opBoolean","COPY",EDGE,{"derivedFrom":makeQuery(id+"F40.opExtrude","SWEPT_EDGE",EDGE,{"disambiguationData":[OSD([subQ2,subQ1,subQ0]),TDD([makeQuery(id+"F39.imprint","INTERSECT",VERTEX,{"disambiguationData":[OD(1.0)],"derivedFrom":[makeQuery(id+"F38.opExtrude","CAP_EDGE",EDGE,{"disambiguationData":[OSD([subQ2])],"isStart":false}),subQ1,subQ0]})])]})});}
            var Q113;
            Q113=makeQuery(id+"F40.boolean.opBoolean","COPY",EDGE,{"derivedFrom":makeQuery(id+"F40.opExtrude","CAP_EDGE",EDGE,{"disambiguationData":[OSD([sQuery(id+"F39.wireOp",EDGE,"E33")])],"isStart":true})});
            var Q114;
            Q114=makeQuery(id+"F40.boolean.opBoolean","COPY",EDGE,{"derivedFrom":makeQuery(id+"F40.opExtrude","CAP_EDGE",EDGE,{"disambiguationData":[OSD([sQuery(id+"F39.wireOp",EDGE,"E33")])],"isStart":false})});
            var Q115;
            Q115=makeQuery(id+"F40.boolean.opBoolean","SPLIT",EDGE,{"disambiguationData":[OD(0.0)],"derivedFrom":makeQuery(id+"F38.opExtrude","CAP_EDGE",EDGE,{"disambiguationData":[OSD([sQuery(id+"F37.wireOp",EDGE,"E32")])],"isStart":false})});
            var Q116;
            Q116=makeQuery(id+"F40.boolean.opBoolean","SPLIT",EDGE,{"disambiguationData":[OD(1.0)],"derivedFrom":makeQuery(id+"F38.opExtrude","CAP_EDGE",EDGE,{"disambiguationData":[OSD([sQuery(id+"F37.wireOp",EDGE,"E32")])],"isStart":false})});
            var Q117;
            Q117=makeQuery(id+"F26.boolean.opBoolean","COPY",EDGE,{"derivedFrom":makeQuery(id+"F26.opExtrude","CAP_EDGE",EDGE,{"disambiguationData":[OSD([sQuery(id+"F25.wireOp",EDGE,"E22")])],"isStart":false})});
            var Q118;
            Q118=makeQuery(id+"F3.boolean.opBoolean","COPY",EDGE,{"derivedFrom":makeQuery(id+"F3.opExtrude","CAP_EDGE",EDGE,{"disambiguationData":[OSD([sQuery(id+"F2.wireOp",EDGE,"E2")])],"isStart":true})});
            var Q119;
            Q119=makeQuery(id+"F5.opExtrude","CAP_EDGE",EDGE,{"disambiguationData":[OSD([sQuery(id+"F4.wireOp",EDGE,"E3")])],"isStart":false});
            var Q120;
            Q120=makeQuery(id+"F5.opExtrude","CAP_EDGE",EDGE,{"disambiguationData":[OSD([sQuery(id+"F4.wireOp",EDGE,"E4")])],"isStart":false});
            var Q121;
            Q121=makeQuery(id+"F5.opExtrude","CAP_EDGE",EDGE,{"disambiguationData":[OSD([sQuery(id+"F4.wireOp",EDGE,"E5.MirrorC")])],"isStart":false});
            var Q122;
            Q122=makeQuery(id+"F5.opExtrude","CAP_EDGE",EDGE,{"disambiguationData":[OSD([sQuery(id+"F4.wireOp",EDGE,"E6.MirrorC")])],"isStart":false});
            var Q123;
            Q123=makeQuery(id+"F8.boolean.opBoolean","INTERSECT",EDGE,{"derivedFrom":[makeQuery(id+"F1.opRevolve","SWEPT_FACE",FACE,{"disambiguationData":[OSD([sQuery(id+"F0.wireOp",EDGE,"E0")])]}),makeQuery(id+"F8.opExtrude","SWEPT_FACE",FACE,{"disambiguationData":[OSD([sQuery(id+"F7.wireOp",EDGE,"E8")])]})]});
            var Q124;
            Q124=makeQuery(id+"F19.boolean.opBoolean","COPY",EDGE,{"derivedFrom":makeQuery(id+"F19.opExtrude","CAP_EDGE",EDGE,{"disambiguationData":[OSD([sQuery(id+"F18.wireOp",EDGE,"E16")])],"isStart":false})});
            var Q125;
            Q125=makeQuery(id+"F33.boolean.opBoolean","COPY",EDGE,{"derivedFrom":makeQuery(id+"F33.opExtrude","CAP_EDGE",EDGE,{"disambiguationData":[OSD([sQuery(id+"F32.wireOp",EDGE,"E28")])],"isStart":false})});
            var Q126;
            Q126=makeQuery(id+"F36.opExtrude","CAP_EDGE",EDGE,{"disambiguationData":[OSD([sQuery(id+"F35.wireOp",EDGE,"E29")])],"isStart":false});
            var Q127;
            Q127=makeQuery(id+"F38.boolean.opBoolean","SPLIT",EDGE,{"disambiguationData":[OD(0.0)],"derivedFrom":makeQuery(id+"F38.opExtrude","CAP_EDGE",EDGE,{"disambiguationData":[OSD([sQuery(id+"F37.wireOp",EDGE,"E32")])],"isStart":true})});
            var Q128;
            Q128=makeQuery(id+"F38.boolean.opBoolean","SPLIT",EDGE,{"disambiguationData":[OD(1.0)],"derivedFrom":makeQuery(id+"F38.opExtrude","CAP_EDGE",EDGE,{"disambiguationData":[OSD([sQuery(id+"F37.wireOp",EDGE,"E32")])],"isStart":true})});
            var Q129;
            Q129=makeQuery(id+"F40.boolean.opBoolean","COPY",EDGE,{"derivedFrom":makeQuery(id+"F40.opExtrude","CAP_EDGE",EDGE,{"disambiguationData":[OSD([sQuery(id+"F39.wireOp",EDGE,"E34")])],"isStart":false})});
            fillet(context, id + "F41", {"entities" : qUnion([Q0, Q1, Q2, Q3, Q4, Q5, Q6, Q7, Q8, Q9, Q10, Q11, Q12, Q13, Q14, Q15, Q16, Q17, Q18, Q19, Q20, Q21, Q22, Q23, Q24, Q25, Q26, Q27, Q28, Q29, Q30, Q31, Q32, Q33, Q34, Q35, Q36, Q37, Q38, Q39, Q40, Q41, Q42, Q43, Q44, Q45, Q46, Q47, Q48, Q49, Q50, Q51, Q52, Q53, Q54, Q55, Q56, Q57, Q58, Q59, Q60, Q61, Q62, Q63, Q64, Q65, Q66, Q67, Q68, Q69, Q70, Q71, Q72, Q73, Q74, Q75, Q76, Q77, Q78, Q79, Q80, Q81, Q82, Q83, Q84, Q85, Q86, Q87, Q88, Q89, Q90, Q91, Q92, Q93, Q94, Q95, Q96, Q97, Q98, Q99, Q100, Q101, Q102, Q103, Q104, Q105, Q106, Q107, Q108, Q109, Q110, Q111, Q112, Q113, Q114, Q115, Q116, Q117, Q118, Q119, Q120, Q121, Q122, Q123, Q124, Q125, Q126, Q127, Q128, Q129]), "radius" : 0.25 * mm, "tangentPropagation" : true, "allowEdgeOverflow" : false});
        }
    });
